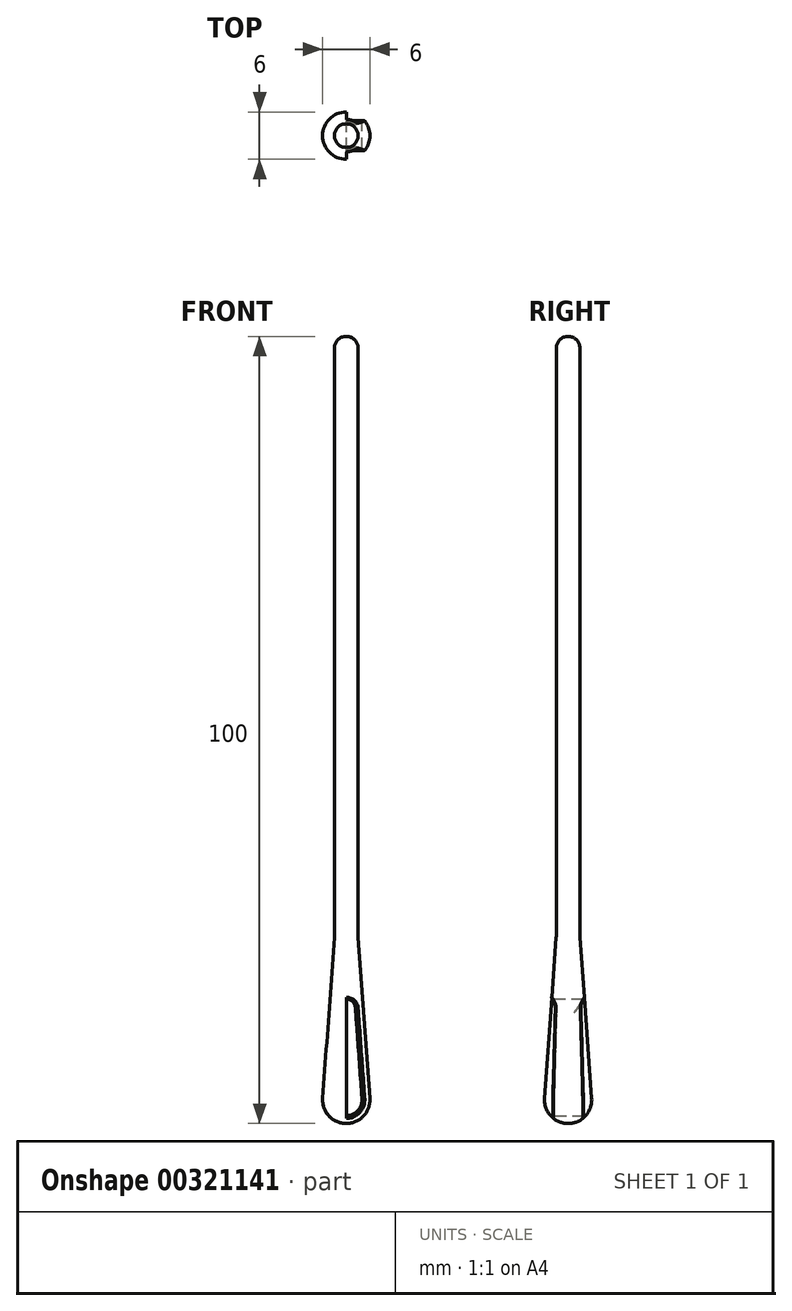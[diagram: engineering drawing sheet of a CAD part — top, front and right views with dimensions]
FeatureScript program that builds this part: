
annotation { "Feature Type Name" : "Feature", "Feature Type Description" : "" }
export const myFeature = defineFeature(function(context is Context, id is Id, definition is map)
    precondition{}
    {
        {
            var Q0;
            Q0=qCreatedBy(makeId("Front.planeOp"),FACE);
            var sketch = newSketch(context, id + "F0", { "sketchPlane" : qUnion([Q0])});
            skLineSegment(sketch, "E0", {"start": v(0, 0) * mm, "end": v(0, 100) * mm});
            skArc(sketch, "E1", {"start": v(1.5, 98.5) * mm, "mid": v(1.06, 99.56) * mm, "end": v(0, 100) * mm});
            skArc(sketch, "E2", {"start": v(0, 0) * mm, "mid": v(2.2, 0.96) * mm, "end": v(3, 3.22) * mm});
            skLineSegment(sketch, "E3", {"start": v(3, 3.22) * mm, "end": v(1.51, 23.63) * mm});
            skLineSegment(sketch, "E4", {"start": v(1.5, 23.99) * mm, "end": v(1.5, 98.5) * mm});
            skPoint(sketch, "E5.visualSharp", {"position": v(1.5, 23.8) * mm});
            skArc(sketch, "E5.filletArc", {"start": v(1.5, 23.99) * mm, "mid": v(1.5, 23.8) * mm, "end": v(1.51, 23.63) * mm});
            skArc(sketch, "E6", {"start": v(0, 1) * mm, "mid": v(1.46, 1.64) * mm, "end": v(2, 3.14) * mm});
            skLineSegment(sketch, "E7", {"start": v(1.15, 14.74) * mm, "end": v(2, 3.14) * mm});
            skPoint(sketch, "E8.orphan", {"position": v(3, -10.62) * mm});
            skArc(sketch, "E9", {"start": v(1.15, 14.74) * mm, "mid": v(0.79, 15.5) * mm, "end": v(0, 15.81) * mm});
            skArc(sketch, "E10.MirrorCS", {"start": v(0, 1) * mm, "mid": v(-1.46, 1.64) * mm, "end": v(-2, 3.14) * mm});
            skLineSegment(sketch, "E11.MirrorCS", {"start": v(-1.15, 14.74) * mm, "end": v(-2, 3.14) * mm});
            skArc(sketch, "E12.MirrorCS", {"start": v(-1.15, 14.74) * mm, "mid": v(-0.79, 15.5) * mm, "end": v(0, 15.81) * mm});
            skSolve(sketch);
        }
        {
            var Q0;
            {var subQ0=sQuery(id+"F0.wireOp",EDGE,"E10.MirrorCS");Q0=makeQuery(id+"F0.imprint","IMPRINT",FACE,{"disambiguationData":[TD([[makeQuery(id+"F0.imprint","IMPRINT",EDGE,{"derivedFrom":subQ0}),-1.0]])]});}
            var Q1;
            {var subQ0=sQuery(id+"F0.wireOp",EDGE,"E6");Q1=makeQuery(id+"F0.imprint","IMPRINT",FACE,{"disambiguationData":[TD([[makeQuery(id+"F0.imprint","IMPRINT",EDGE,{"derivedFrom":subQ0}),1.0]])]});}
            extrude(context, id + "F1", {"entities" : qUnion([Q0, Q1]), "endBound" : BoundingType.SYMMETRIC, "depth" : 25 * mm});
        }
        {
            var Q0;
            Q0=makeQuery(id+"F0.imprint","IMPRINT",FACE,{"disambiguationData":[TD([[makeQuery(id+"F0.imprint","IMPRINT",EDGE,{"derivedFrom":sQuery(id+"F0.wireOp",EDGE,"E0")}),-1.0]])]});
            var Q1;
            {var subQ0=sQuery(id+"F0.wireOp",EDGE,"E6");Q1=makeQuery(id+"F0.imprint","IMPRINT",FACE,{"disambiguationData":[TD([[makeQuery(id+"F0.imprint","IMPRINT",EDGE,{"derivedFrom":subQ0}),1.0]])]});}
            var Q2;
            Q2=sQuery(id+"F0.wireOp",EDGE,"E0");
            revolve(context, id + "F2", {"entities" : qUnion([Q0, Q1]), "axis" : qUnion([Q2]), "revolveType" : RevolveType.FULL});
        }
        {
            var Q0;
            Q0=makeQuery(id+"F1.opExtrude","SWEPT_BODY",BODY,{"disambiguationData":[OSD([sQuery(id+"F0.wireOp",EDGE,"E6"),sQuery(id+"F0.wireOp",EDGE,"E7"),sQuery(id+"F0.wireOp",EDGE,"E9"),sQuery(id+"F0.wireOp",EDGE,"E10.MirrorCS"),sQuery(id+"F0.wireOp",EDGE,"E11.MirrorCS"),sQuery(id+"F0.wireOp",EDGE,"E12.MirrorCS")])]});
            var Q1;
            Q1=makeQuery(id+"F2.opRevolve","SWEPT_BODY",BODY,{"disambiguationData":[OSD([sQuery(id+"F0.wireOp",EDGE,"E0"),sQuery(id+"F0.wireOp",EDGE,"E1"),sQuery(id+"F0.wireOp",EDGE,"E2"),sQuery(id+"F0.wireOp",EDGE,"E3"),sQuery(id+"F0.wireOp",EDGE,"E4"),sQuery(id+"F0.wireOp",EDGE,"E5.filletArc")])]});
            booleanBodies(context, id + "F3", {"operationType" : BooleanOperationType.SUBTRACTION, "tools" : qUnion([Q0]), "targets" : qUnion([Q1])});
        }
        {
            var Q0;
            Q0=makeQuery(id+"F3.opBoolean","INTERSECT",EDGE,{"disambiguationData":[OD(0.0)],"derivedFrom":[makeQuery(id+"F1.opExtrude","SWEPT_FACE",FACE,{"disambiguationData":[OSD([sQuery(id+"F0.wireOp",EDGE,"E11.MirrorCS")])]}),makeQuery(id+"F2.opRevolve","SWEPT_FACE",FACE,{"disambiguationData":[OSD([sQuery(id+"F0.wireOp",EDGE,"E3")])]})]});
            var Q1;
            Q1=makeQuery(id+"F3.opBoolean","INTERSECT",EDGE,{"disambiguationData":[OD(0.0)],"derivedFrom":[makeQuery(id+"F1.opExtrude","SWEPT_FACE",FACE,{"disambiguationData":[OSD([sQuery(id+"F0.wireOp",EDGE,"E9"),sQuery(id+"F0.wireOp",EDGE,"E12.MirrorCS")])]}),makeQuery(id+"F2.opRevolve","SWEPT_FACE",FACE,{"disambiguationData":[OSD([sQuery(id+"F0.wireOp",EDGE,"E3")])]})]});
            var Q2;
            Q2=makeQuery(id+"F3.opBoolean","INTERSECT",EDGE,{"disambiguationData":[OD(0.0)],"derivedFrom":[makeQuery(id+"F1.opExtrude","SWEPT_FACE",FACE,{"disambiguationData":[OSD([sQuery(id+"F0.wireOp",EDGE,"E7")])]}),makeQuery(id+"F2.opRevolve","SWEPT_FACE",FACE,{"disambiguationData":[OSD([sQuery(id+"F0.wireOp",EDGE,"E3")])]})]});
            var Q3;
            Q3=makeQuery(id+"F3.opBoolean","INTERSECT",EDGE,{"disambiguationData":[OD(0.0)],"derivedFrom":[makeQuery(id+"F1.opExtrude","SWEPT_FACE",FACE,{"disambiguationData":[OSD([sQuery(id+"F0.wireOp",EDGE,"E6"),sQuery(id+"F0.wireOp",EDGE,"E10.MirrorCS")])]}),makeQuery(id+"F2.opRevolve","SWEPT_FACE",FACE,{"disambiguationData":[OSD([sQuery(id+"F0.wireOp",EDGE,"E2")])]})]});
            var Q4;
            Q4=makeQuery(id+"F3.opBoolean","INTERSECT",EDGE,{"disambiguationData":[OD(1.0)],"derivedFrom":[makeQuery(id+"F1.opExtrude","SWEPT_FACE",FACE,{"disambiguationData":[OSD([sQuery(id+"F0.wireOp",EDGE,"E7")])]}),makeQuery(id+"F2.opRevolve","SWEPT_FACE",FACE,{"disambiguationData":[OSD([sQuery(id+"F0.wireOp",EDGE,"E3")])]})]});
            var Q5;
            Q5=makeQuery(id+"F3.opBoolean","INTERSECT",EDGE,{"disambiguationData":[OD(1.0)],"derivedFrom":[makeQuery(id+"F1.opExtrude","SWEPT_FACE",FACE,{"disambiguationData":[OSD([sQuery(id+"F0.wireOp",EDGE,"E6"),sQuery(id+"F0.wireOp",EDGE,"E10.MirrorCS")])]}),makeQuery(id+"F2.opRevolve","SWEPT_FACE",FACE,{"disambiguationData":[OSD([sQuery(id+"F0.wireOp",EDGE,"E2")])]})]});
            var Q6;
            Q6=makeQuery(id+"F3.opBoolean","INTERSECT",EDGE,{"disambiguationData":[OD(1.0)],"derivedFrom":[makeQuery(id+"F1.opExtrude","SWEPT_FACE",FACE,{"disambiguationData":[OSD([sQuery(id+"F0.wireOp",EDGE,"E11.MirrorCS")])]}),makeQuery(id+"F2.opRevolve","SWEPT_FACE",FACE,{"disambiguationData":[OSD([sQuery(id+"F0.wireOp",EDGE,"E3")])]})]});
            var Q7;
            Q7=makeQuery(id+"F3.opBoolean","INTERSECT",EDGE,{"disambiguationData":[OD(1.0)],"derivedFrom":[makeQuery(id+"F1.opExtrude","SWEPT_FACE",FACE,{"disambiguationData":[OSD([sQuery(id+"F0.wireOp",EDGE,"E9"),sQuery(id+"F0.wireOp",EDGE,"E12.MirrorCS")])]}),makeQuery(id+"F2.opRevolve","SWEPT_FACE",FACE,{"disambiguationData":[OSD([sQuery(id+"F0.wireOp",EDGE,"E3")])]})]});
            fillet(context, id + "F4", {"entities" : qUnion([Q0, Q1, Q2, Q3, Q4, Q5, Q6, Q7]), "radius" : 0.2 * mm, "tangentPropagation" : true, "allowEdgeOverflow" : false});
        }
    });
